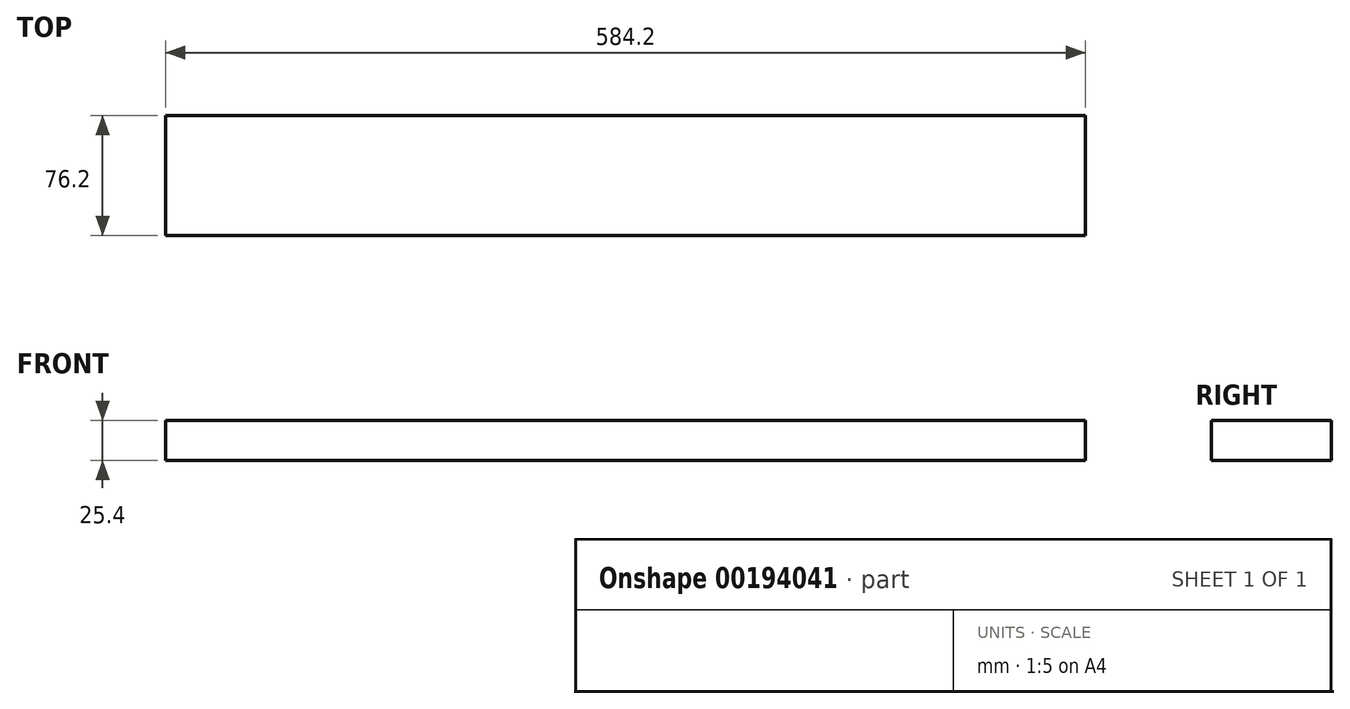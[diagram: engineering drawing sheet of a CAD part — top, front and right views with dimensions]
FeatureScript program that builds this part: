
annotation { "Feature Type Name" : "Feature", "Feature Type Description" : "" }
export const myFeature = defineFeature(function(context is Context, id is Id, definition is map)
    precondition{}
    {
        {
            var Q0;
            Q0=qCreatedBy(makeId("Top.planeOp"),FACE);
            var sketch = newSketch(context, id + "F0", { "sketchPlane" : qUnion([Q0])});
            skLineSegment(sketch, "E0.bottom", {"start": v(292.1, 38.1) * mm, "end": v(-292.1, 38.1) * mm});
            skLineSegment(sketch, "E0.top", {"start": v(292.1, -38.1) * mm, "end": v(-292.1, -38.1) * mm});
            skLineSegment(sketch, "E0.left", {"start": v(292.1, 38.1) * mm, "end": v(292.1, -38.1) * mm});
            skLineSegment(sketch, "E0.right", {"start": v(-292.1, 38.1) * mm, "end": v(-292.1, -38.1) * mm});
            skPoint(sketch, "E0.middle", {"position": v(0, 0) * mm});
            skSolve(sketch);
        }
        {
            var Q0;
            Q0=makeQuery(id+"F0.imprint","IMPRINT",FACE,{"disambiguationData":[TD([[makeQuery(id+"F0.imprint","IMPRINT",EDGE,{"derivedFrom":sQuery(id+"F0.wireOp",EDGE,"E0.bottom")}),1.0]])]});
            extrude(context, id + "F1", {"entities" : qUnion([Q0]), "depth" : 25.4 * mm});
        }
    });
